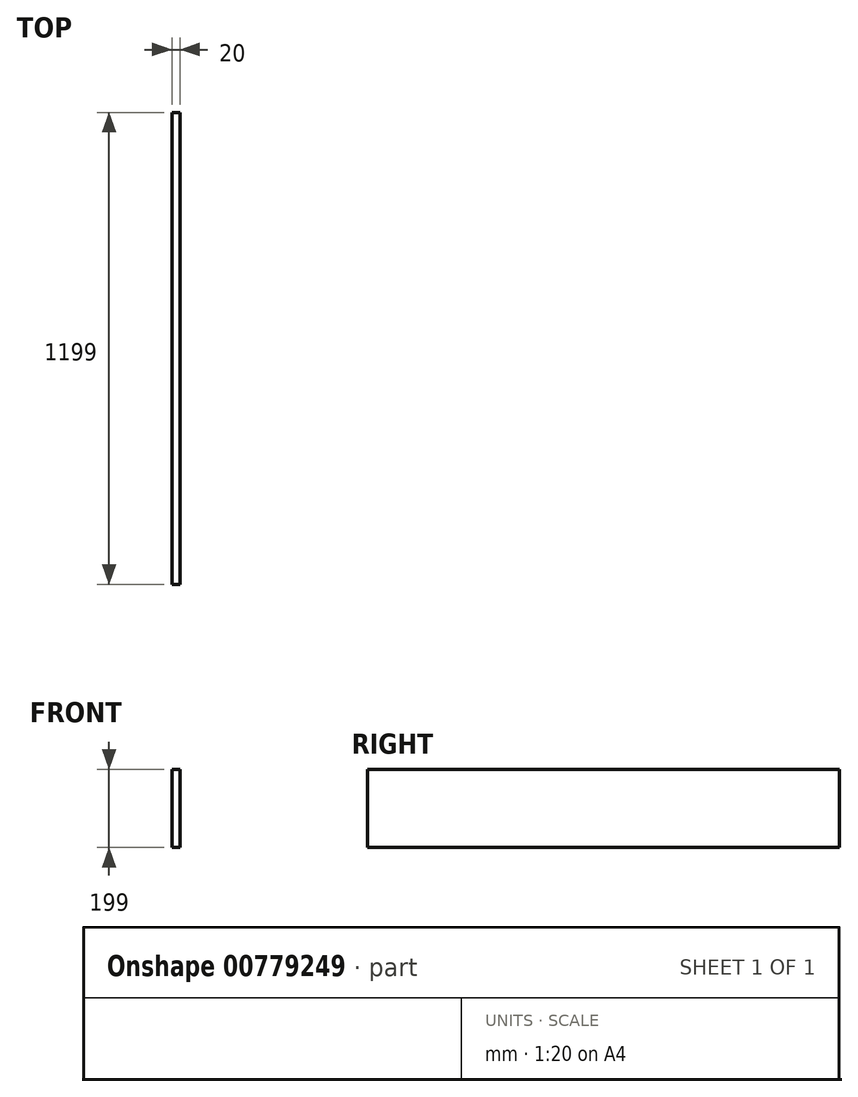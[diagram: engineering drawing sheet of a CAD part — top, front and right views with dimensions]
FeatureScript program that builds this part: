
annotation { "Feature Type Name" : "Feature", "Feature Type Description" : "" }
export const myFeature = defineFeature(function(context is Context, id is Id, definition is map)
    precondition{}
    {
        {
            var Q0;
            Q0=qCreatedBy(makeId("Front.planeOp"),FACE);
            var sketch = newSketch(context, id + "F0", { "sketchPlane" : qUnion([Q0])});
            skLineSegment(sketch, "E0.bottom", {"start": v(0, 0) * mm, "end": v(20, 0) * mm});
            skLineSegment(sketch, "E0.top", {"start": v(0, 199) * mm, "end": v(20, 199) * mm});
            skLineSegment(sketch, "E0.left", {"start": v(0, 0) * mm, "end": v(0, 199) * mm});
            skLineSegment(sketch, "E0.right", {"start": v(20, 0) * mm, "end": v(20, 199) * mm});
            skSolve(sketch);
        }
        {
            var Q0;
            Q0=qSketchRegion(id+"F0",true);
            extrude(context, id + "F1", {"entities" : qUnion([Q0]), "depth" : 1199 * mm});
        }
    });
